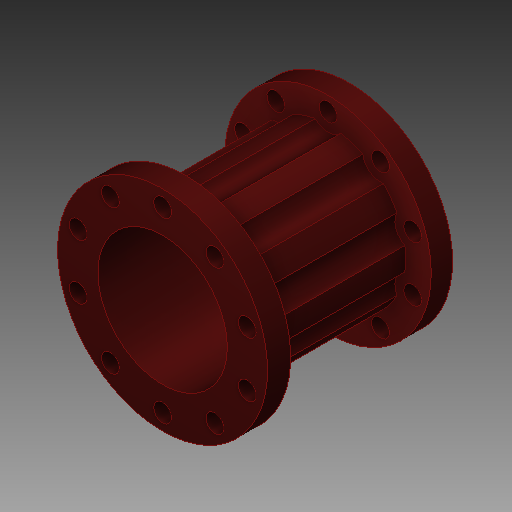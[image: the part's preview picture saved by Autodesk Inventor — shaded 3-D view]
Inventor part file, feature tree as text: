
AUTODESK INVENTOR PART (.ipt)
format: ipt  version: 2019 (Build 230136000, 136)  size: 314,368 bytes
history: native  units: mm
features: sketch x5, extrude x3, pattern_circular x2, fillet x1, hole x1, revolve x1, projected_geometry x1
ambient origin geometry x8: Origin, YZ Plane, XZ Plane, XY Plane, X Axis, Y Axis, Z Axis, Center Point
bodies: Solid1 (feature_tree)
feature tree (14):
  extrude  "Extrusion1"  Depth=36.376mm
  extrude  "Extrusion2"  Depth=59.0mm
  extrude  "Extrusion3"  Depth=58.0mm
  fillet  "Fillet1"  Radius=6.0mm
  hole  "Hole1"  [1 undecoded]
  pattern_circular  "Circular Pattern1"  Count=10 Angle=360.0deg
  revolve  "Revolution1"  [1 undecoded]
  pattern_circular  "Circular Pattern2"  [2 undecoded]
  sketch  "Sketch1"  dims[d1=43.646mm d2=36.376mm]
  sketch  "Sketch2"  dims[d3=40.0mm d4=0.0mm d5=59.0mm]
  sketch  "Sketch3"  dims[d6=6.5mm d7=0.0mm d8=58.0mm d9=6.0mm d10=0.0mm]
  sketch  "Sketch4"  dims[d11=2.0mm d12=25.0mm]
  sketch  "Sketch6"  dims[d13=5.0mm d14=6.0mm d15=4.0mm d16=2.0mm d17=90.0deg d18=8.0mm d19=20.594885mm d20=100.0mm d21=360.0deg d27=5.0mm d28=5.0mm d29=40.0mm d31=90.0deg d32=100.0mm d33=360.0deg]
  projected_geometry  "Project Cut Edges1"
note: 4 required parameter values undecoded (feature->parameter linkage not recoverable at this tier; creation-order binding heuristic only, values carry confidence <= 0.55)